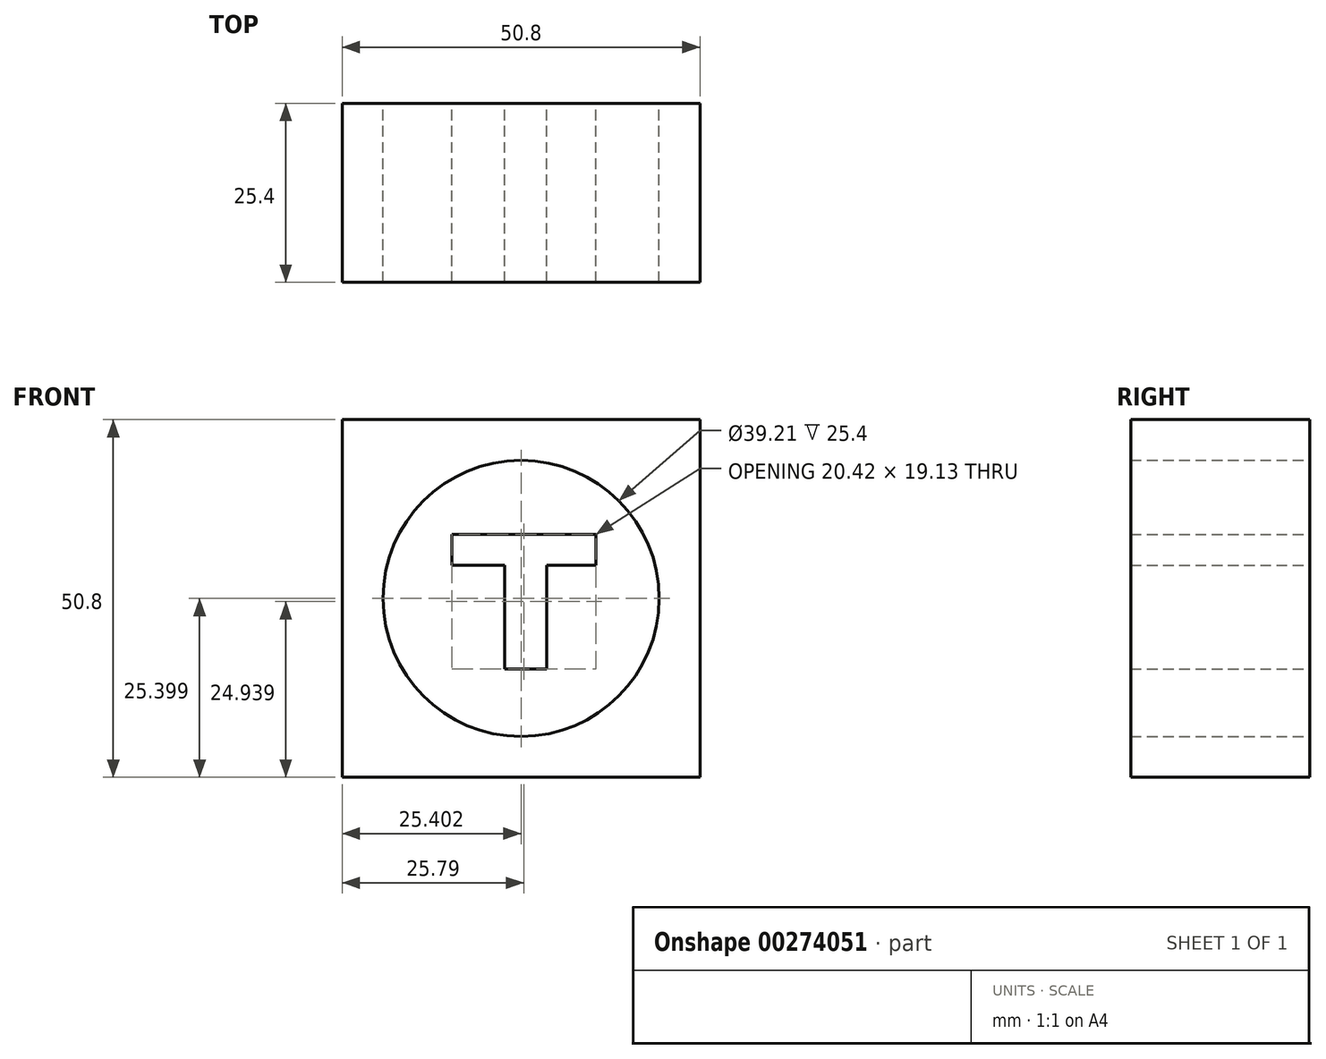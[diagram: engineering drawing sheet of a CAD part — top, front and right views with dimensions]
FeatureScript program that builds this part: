
annotation { "Feature Type Name" : "Feature", "Feature Type Description" : "" }
export const myFeature = defineFeature(function(context is Context, id is Id, definition is map)
    precondition{}
    {
        {
            var Q0;
            Q0=qCreatedBy(makeId("Front.planeOp"),FACE);
            var sketch = newSketch(context, id + "F0", { "sketchPlane" : qUnion([Q0])});
            skLineSegment(sketch, "E0", {"start": v(-32.64, 27.8) * mm, "end": v(18.16, 27.8) * mm});
            skLineSegment(sketch, "E1", {"start": v(18.16, 27.8) * mm, "end": v(18.16, -23) * mm});
            skLineSegment(sketch, "E2", {"start": v(18.16, -23) * mm, "end": v(-32.64, -23) * mm});
            skLineSegment(sketch, "E3", {"start": v(-32.64, -23) * mm, "end": v(-32.64, 27.8) * mm});
            skPoint(sketch, "E4.endSnap0", {"position": v(-7.24, -23) * mm});
            skLineSegment(sketch, "E5", {"start": v(-17.06, 11.5) * mm, "end": v(-17.06, 7.1) * mm});
            skLineSegment(sketch, "E6", {"start": v(-17.06, 7.1) * mm, "end": v(-9.56, 7.1) * mm});
            skLineSegment(sketch, "E7", {"start": v(-9.56, 7.1) * mm, "end": v(-9.56, -7.63) * mm});
            skLineSegment(sketch, "E8", {"start": v(-9.56, -7.63) * mm, "end": v(-3.62, -7.63) * mm});
            skLineSegment(sketch, "E9", {"start": v(-3.62, -7.63) * mm, "end": v(-3.62, 7.1) * mm});
            skLineSegment(sketch, "E10", {"start": v(-3.62, 7.1) * mm, "end": v(3.36, 7.1) * mm});
            skLineSegment(sketch, "E11", {"start": v(3.36, 7.1) * mm, "end": v(3.36, 11.5) * mm});
            skLineSegment(sketch, "E12", {"start": v(3.36, 11.5) * mm, "end": v(-17.06, 11.5) * mm});
            skCircle(sketch, "E13", {"center": v(-7.24, 2.4) * mm, "radius": 19.6 * mm});
            skSolve(sketch);
        }
        {
            var Q0;
            Q0=makeQuery(id+"F0.imprint","IMPRINT",FACE,{"disambiguationData":[TD([[makeQuery(id+"F0.imprint","IMPRINT",EDGE,{"derivedFrom":sQuery(id+"F0.wireOp",EDGE,"E0")}),-1.0]])]});
            var Q1;
            Q1=makeQuery(id+"F0.imprint","IMPRINT",FACE,{"disambiguationData":[TD([[makeQuery(id+"F0.imprint","IMPRINT",EDGE,{"derivedFrom":sQuery(id+"F0.wireOp",EDGE,"E5")}),1.0]])]});
            extrude(context, id + "F1", {"entities" : qUnion([Q0, Q1]), "depth" : 25.4 * mm});
        }
        {
            var Q0;
            Q0=makeQuery(id+"F0.imprint","IMPRINT",FACE,{"disambiguationData":[TD([[makeQuery(id+"F0.imprint","IMPRINT",EDGE,{"derivedFrom":sQuery(id+"F0.wireOp",EDGE,"E0")}),-1.0]])]});
            var Q1;
            Q1=makeQuery(id+"F0.imprint","IMPRINT",FACE,{"disambiguationData":[TD([[makeQuery(id+"F0.imprint","IMPRINT",EDGE,{"derivedFrom":sQuery(id+"F0.wireOp",EDGE,"E5")}),-1.0]])]});
            extrude(context, id + "F2", {"entities" : qUnion([Q0, Q1]), "depth" : 25.4 * mm});
        }
    });
